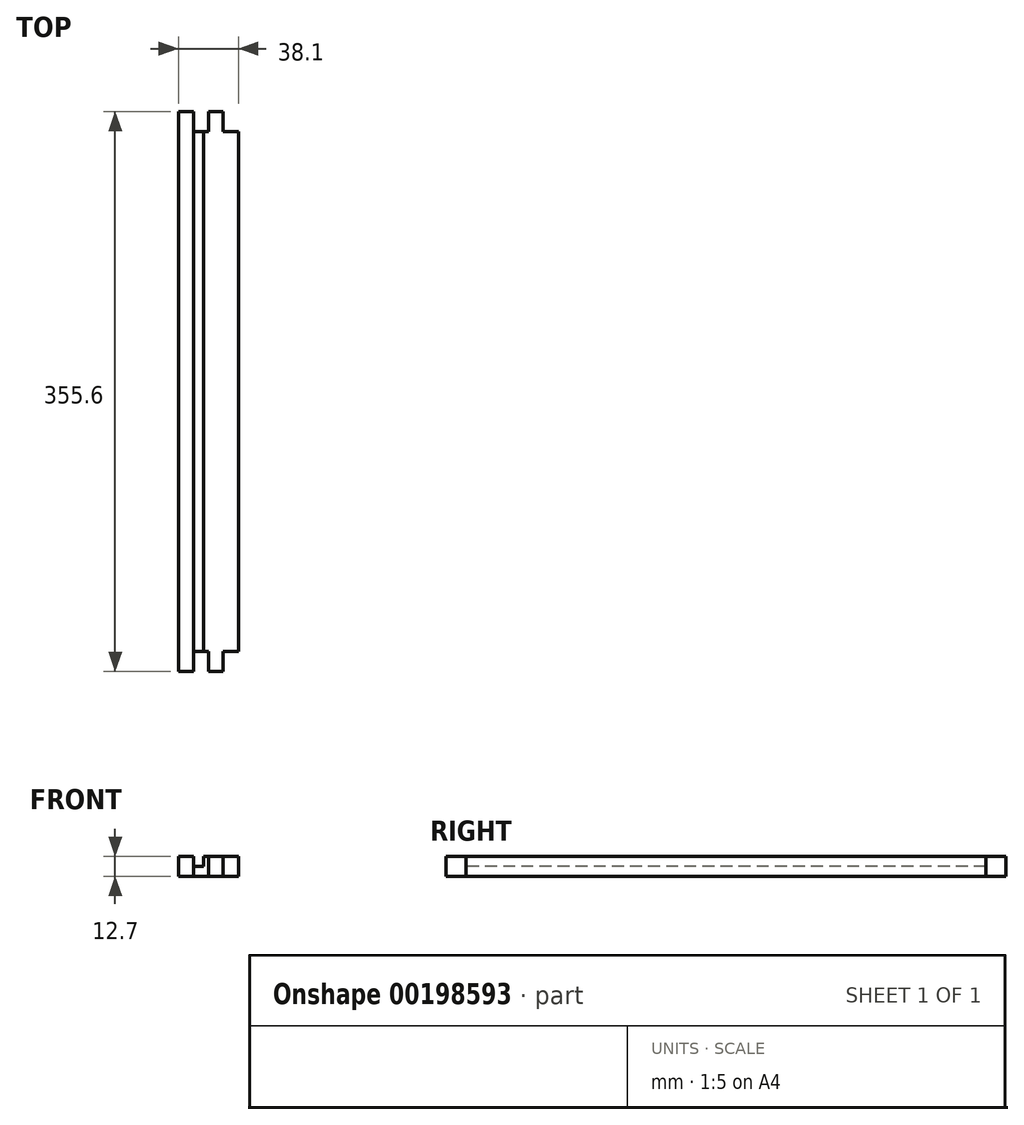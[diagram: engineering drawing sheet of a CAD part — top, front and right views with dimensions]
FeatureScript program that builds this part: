
annotation { "Feature Type Name" : "Feature", "Feature Type Description" : "" }
export const myFeature = defineFeature(function(context is Context, id is Id, definition is map)
    precondition{}
    {
        {
            var Q0;
            Q0=qCreatedBy(makeId("Front.planeOp"),FACE);
            var sketch = newSketch(context, id + "F0", { "sketchPlane" : qUnion([Q0])});
            skLineSegment(sketch, "E0.bottom", {"start": v(0, 0) * mm, "end": v(38.1, 0) * mm});
            skLineSegment(sketch, "E0.top", {"start": v(0, 12.7) * mm, "end": v(38.1, 12.7) * mm});
            skLineSegment(sketch, "E0.left", {"start": v(0, 0) * mm, "end": v(0, 12.7) * mm});
            skLineSegment(sketch, "E0.right", {"start": v(38.1, 0) * mm, "end": v(38.1, 12.7) * mm});
            skSolve(sketch);
        }
        {
            var Q0;
            Q0 = qSketchRegion(id + "F0", true);
            extrude(context, id + "F1", {"entities" : qUnion([Q0]), "depth" : 355.6 * mm});
        }
        {
            var Q0;
            Q0=makeQuery(id+"F1.opExtrude","CAP_FACE",FACE,{"disambiguationData":[OSD([sQuery(id+"F0.wireOp",EDGE,"E0.bottom"),sQuery(id+"F0.wireOp",EDGE,"E0.top"),sQuery(id+"F0.wireOp",EDGE,"E0.left"),sQuery(id+"F0.wireOp",EDGE,"E0.right")])],"isStart":false});
            var sketch = newSketch(context, id + "F2", { "sketchPlane" : qUnion([Q0])});
            skLineSegment(sketch, "E1", {"start": v(9.53, 12.7) * mm, "end": v(9.53, 6.35) * mm});
            skLineSegment(sketch, "E2", {"start": v(9.53, 6.35) * mm, "end": v(15.88, 6.35) * mm});
            skLineSegment(sketch, "E3", {"start": v(15.88, 6.35) * mm, "end": v(15.88, 12.7) * mm});
            skLineSegment(sketch, "E4", {"start": v(15.88, 12.7) * mm, "end": v(9.53, 12.7) * mm});
            skSolve(sketch);
        }
        {
            var Q0;
            Q0 = qSketchRegion(id + "F2", true);
            extrude(context, id + "F3", {"entities" : qUnion([Q0]), "operationType" : NewBodyOperationType.REMOVE, "endBound" : BoundingType.THROUGH_ALL, "oppositeDirection" : true, "depth" : 25.4 * mm});
        }
        {
            var Q0;
            Q0=makeQuery(id+"F1.opExtrude","SWEPT_FACE",FACE,{"disambiguationData":[OSD([sQuery(id+"F0.wireOp",EDGE,"E0.bottom")])]});
            var sketch = newSketch(context, id + "F4", { "sketchPlane" : qUnion([Q0])});
            skLineSegment(sketch, "E5.bottom", {"start": v(38.1, 355.6) * mm, "end": v(28.58, 355.6) * mm});
            skLineSegment(sketch, "E5.top", {"start": v(38.1, 342.9) * mm, "end": v(28.58, 342.9) * mm});
            skLineSegment(sketch, "E5.left", {"start": v(38.1, 355.6) * mm, "end": v(38.1, 342.9) * mm});
            skLineSegment(sketch, "E5.right", {"start": v(28.58, 355.6) * mm, "end": v(28.58, 342.9) * mm});
            skLineSegment(sketch, "E6", {"start": v(19.05, 355.6) * mm, "end": v(19.05, 342.9) * mm});
            skLineSegment(sketch, "E7", {"start": v(19.05, 342.9) * mm, "end": v(9.53, 342.9) * mm});
            skLineSegment(sketch, "E8", {"start": v(9.53, 342.9) * mm, "end": v(9.53, 355.6) * mm});
            skLineSegment(sketch, "E9", {"start": v(9.53, 355.6) * mm, "end": v(19.05, 355.6) * mm});
            skLineSegment(sketch, "E10.MirrorCS", {"start": v(28.58, 0) * mm, "end": v(28.58, 12.7) * mm});
            skLineSegment(sketch, "E11.MirrorCS", {"start": v(9.53, 12.7) * mm, "end": v(9.53, 0) * mm});
            skLineSegment(sketch, "E12.MirrorCS", {"start": v(19.05, 0) * mm, "end": v(19.05, 12.7) * mm});
            skLineSegment(sketch, "E13.MirrorCS", {"start": v(9.53, 0) * mm, "end": v(19.05, 0) * mm});
            skLineSegment(sketch, "E14.MirrorCS", {"start": v(38.1, 0) * mm, "end": v(38.1, 12.7) * mm});
            skLineSegment(sketch, "E15.MirrorCS", {"start": v(38.1, 12.7) * mm, "end": v(28.58, 12.7) * mm});
            skLineSegment(sketch, "E16.MirrorCS", {"start": v(38.1, 0) * mm, "end": v(28.58, 0) * mm});
            skLineSegment(sketch, "E17.MirrorCS", {"start": v(19.05, 12.7) * mm, "end": v(9.53, 12.7) * mm});
            skSolve(sketch);
        }
        {
            var Q0;
            Q0 = qSketchRegion(id + "F4", true);
            extrude(context, id + "F5", {"entities" : qUnion([Q0]), "operationType" : NewBodyOperationType.REMOVE, "endBound" : BoundingType.THROUGH_ALL, "oppositeDirection" : true, "depth" : 25.4 * mm});
        }
    });
